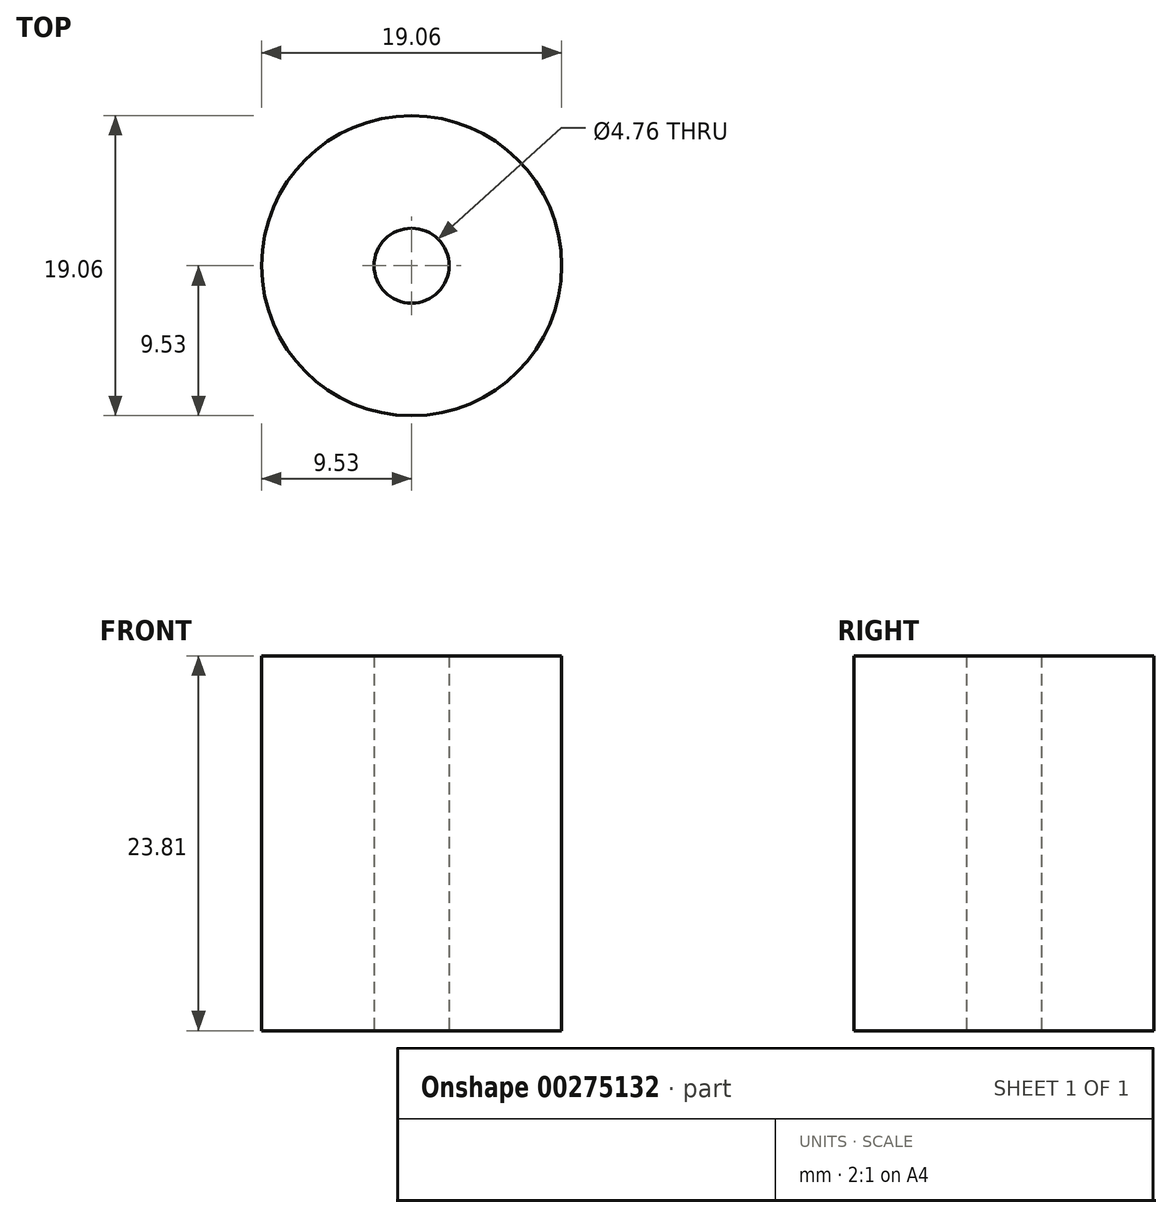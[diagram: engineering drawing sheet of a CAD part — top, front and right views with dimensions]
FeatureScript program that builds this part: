
annotation { "Feature Type Name" : "Feature", "Feature Type Description" : "" }
export const myFeature = defineFeature(function(context is Context, id is Id, definition is map)
    precondition{}
    {
        {
            var Q0;
            Q0=qCreatedBy(makeId("Top.planeOp"),FACE);
            var sketch = newSketch(context, id + "F0", { "sketchPlane" : qUnion([Q0])});
            skCircle(sketch, "E0", {"center": v(0, 0) * mm, "radius": 9.53 * mm});
            skCircle(sketch, "E1", {"center": v(0, 0) * mm, "radius": 2.38 * mm});
            skSolve(sketch);
        }
        {
            var Q0;
            Q0 = qSketchRegion(id + "F0", true);
            extrude(context, id + "F1", {"entities" : qUnion([Q0]), "depth" : 23.8 * mm});
        }
    });
